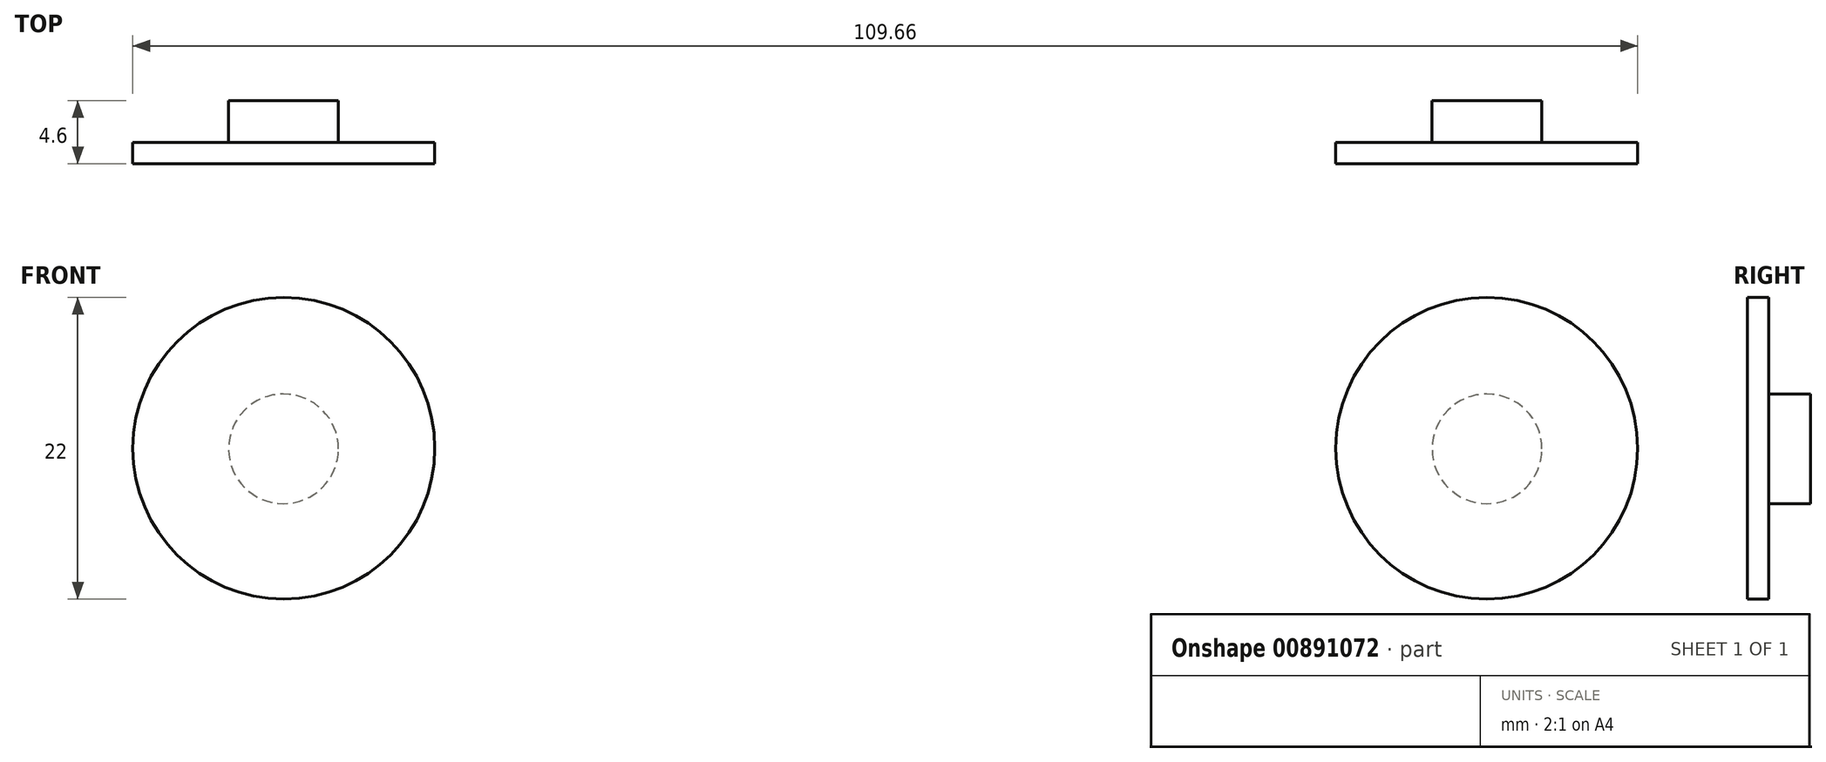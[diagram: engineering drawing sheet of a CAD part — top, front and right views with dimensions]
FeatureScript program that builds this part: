
annotation { "Feature Type Name" : "Feature", "Feature Type Description" : "" }
export const myFeature = defineFeature(function(context is Context, id is Id, definition is map)
    precondition{}
    {
        {
            var Q0;
            Q0=qCreatedBy(makeId("Front.planeOp"),FACE);
            var sketch = newSketch(context, id + "F0", { "sketchPlane" : qUnion([Q0])});
            skCircle(sketch, "E0", {"center": v(-43.85, 37.33) * mm, "radius": 4 * mm});
            skSolve(sketch);
        }
        {
            var Q0;
            Q0=makeQuery(id+"F0.imprint","IMPRINT",FACE,{"disambiguationData":[TD([[makeQuery(id+"F0.imprint","IMPRINT",EDGE,{"derivedFrom":sQuery(id+"F0.wireOp",EDGE,"E0")}),1.0]])]});
            extrude(context, id + "F1", {"entities" : qUnion([Q0]), "depth" : 4.06 * mm, "offsetDistance" : 25.4 * mm});
        }
        {
            var Q0;
            Q0=makeQuery(id+"F1.opExtrude","SWEPT_BODY",BODY,{"disambiguationData":[OSD([sQuery(id+"F0.wireOp",EDGE,"E0")])]});
            var Q1;
            Q1=qCreatedBy(makeId("Right.planeOp"),FACE);
            mirror(context, id + "F2", {"entities" : qUnion([Q0]), "mirrorPlane" : qUnion([Q1])});
        }
        {
            var Q0;
            Q0=qCreatedBy(makeId("Front.planeOp"),FACE);
            cPlane(context, id + "F3", {"entities" : qUnion([Q0]), "cplaneType" : CPlaneType.OFFSET, "offset" : 3.05 * mm, "width" : 152.4 * mm, "height" : 152.4 * mm});
        }
        {
            var Q0;
            Q0=qCreatedBy(id+"F3.planeOp",FACE);
            var sketch = newSketch(context, id + "F4", { "sketchPlane" : qUnion([Q0])});
            skPoint(sketch, "E1.first.point", {"position": v(-47, 41.24) * mm});
            skPoint(sketch, "E1.second.point", {"position": v(-39.92, 40.48) * mm});
            skPoint(sketch, "E1.third.point", {"position": v(-43.81, 32.37) * mm});
            skCircle(sketch, "E2", {"center": v(-43.83, 37.37) * mm, "radius": 11 * mm});
            skSolve(sketch);
        }
        {
            var Q0;
            Q0=makeQuery(id+"F4.imprint","IMPRINT",FACE,{"disambiguationData":[TD([[makeQuery(id+"F4.imprint","IMPRINT",EDGE,{"derivedFrom":sQuery(id+"F4.wireOp",EDGE,"E2")}),1.0]])]});
            extrude(context, id + "F5", {"entities" : qUnion([Q0]), "operationType" : NewBodyOperationType.ADD, "depth" : 1.55 * mm, "offsetDistance" : 25.4 * mm});
        }
        {
            var Q0;
            Q0=makeQuery(id+"F1.opExtrude","SWEPT_BODY",BODY,{"disambiguationData":[OSD([sQuery(id+"F0.wireOp",EDGE,"E0")])]});
            var Q1;
            Q1=qCreatedBy(makeId("Right.planeOp"),FACE);
            mirror(context, id + "F6", {"operationType" : NewBodyOperationType.ADD, "entities" : qUnion([Q0]), "mirrorPlane" : qUnion([Q1])});
        }
    });
